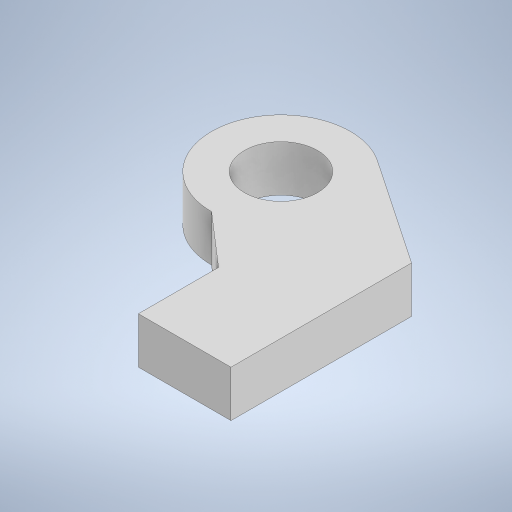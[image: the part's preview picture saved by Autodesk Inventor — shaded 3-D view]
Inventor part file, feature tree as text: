
AUTODESK INVENTOR PART (.ipt)
format: ipt  version: 2024 (Build 280153000, 153)  size: 245,760 bytes
history: native  units: mm
features: sketch x4, extrude x3
ambient origin geometry x8: Origin, YZ Plane, XZ Plane, XY Plane, X Axis, Y Axis, Z Axis, Center Point
bodies: Solid1 (feature_tree)
feature tree (7):
  extrude  "Extrusion1"  Depth=31.197mm
  sketch  "Sketch2"  dims[d2=42.0mm d4=10.0mm d5=0.0mm]
  extrude  "Extrusion2"  Depth=10.0mm TaperAngle=0.0deg
  extrude  "Extrusion3"  Depth=10.0mm TaperAngle=0.0deg
  sketch  "Sketch1"  dims[d0=15.8mm d1=31.197mm]
  sketch  "Sketch3"  dims[d7=10.0mm d8=0.0mm d9=10.0mm d10=0.0mm]
  sketch  "Sketch4"
